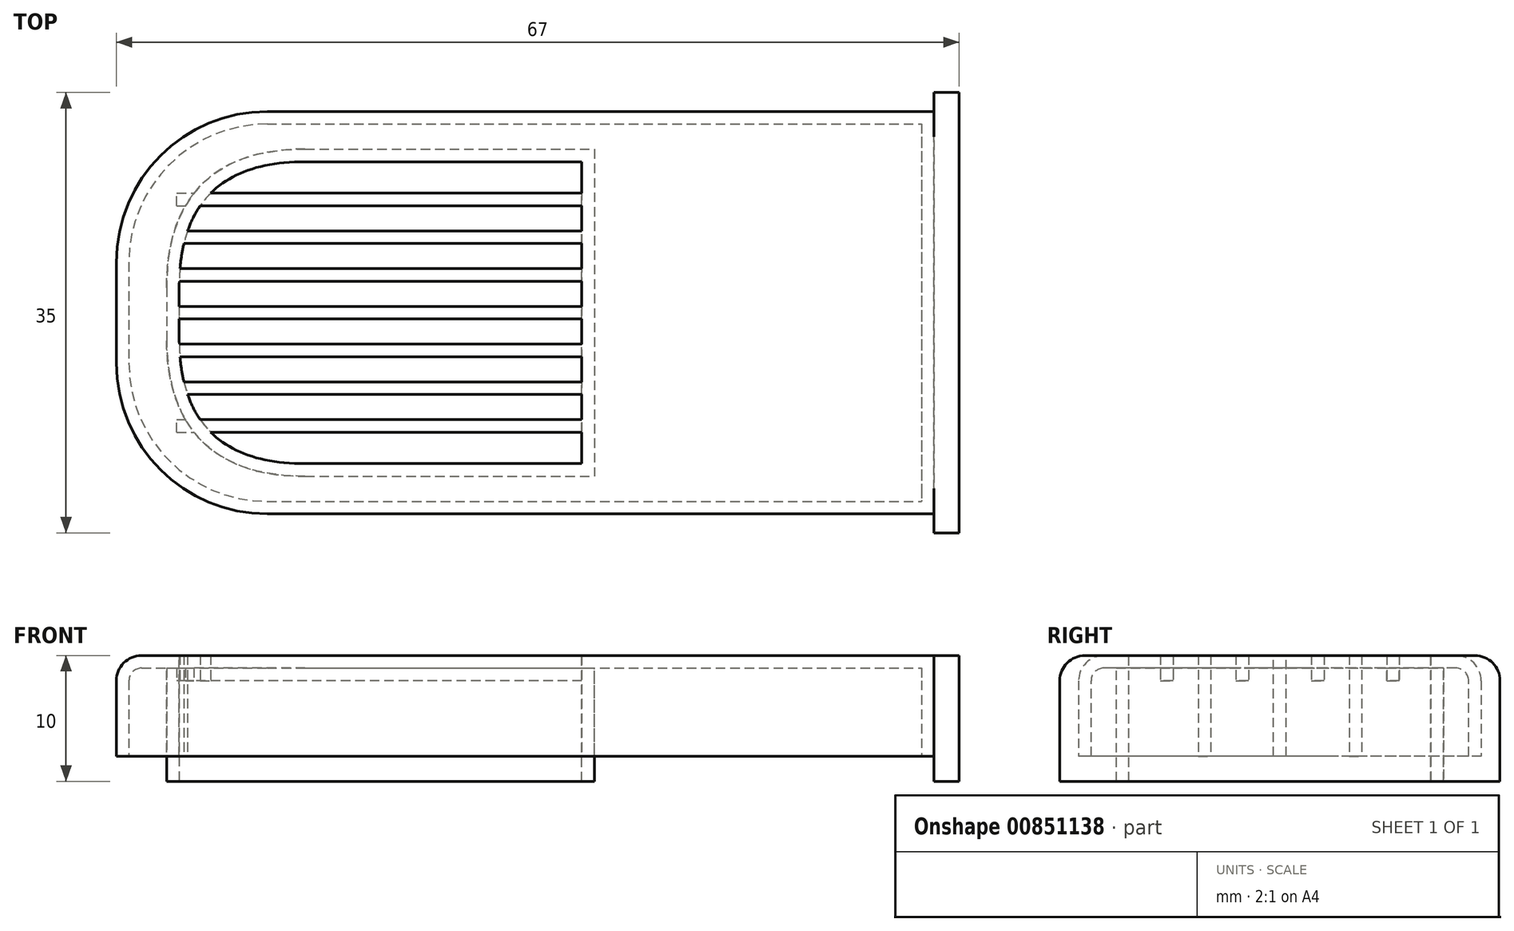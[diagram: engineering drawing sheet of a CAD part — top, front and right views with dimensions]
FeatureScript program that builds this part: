
annotation { "Feature Type Name" : "Feature", "Feature Type Description" : "" }
export const myFeature = defineFeature(function(context is Context, id is Id, definition is map)
    precondition{}
    {
        {
            var Q0;
            Q0=qCreatedBy(makeId("Top.planeOp"),FACE);
            var sketch = newSketch(context, id + "F0", { "sketchPlane" : qUnion([Q0])});
            skLineSegment(sketch, "E0.bottom", {"start": v(-32.5, 16) * mm, "end": v(32.5, 16) * mm});
            skLineSegment(sketch, "E0.top", {"start": v(-32.5, -16) * mm, "end": v(32.5, -16) * mm});
            skLineSegment(sketch, "E0.left", {"start": v(-32.5, 16) * mm, "end": v(-32.5, -16) * mm});
            skLineSegment(sketch, "E0.right", {"start": v(32.5, 16) * mm, "end": v(32.5, -16) * mm});
            skPoint(sketch, "E0.middle", {"position": v(0, 0) * mm});
            skSolve(sketch);
        }
        {
            var Q0;
            Q0=makeQuery(id+"F0.imprint","IMPRINT",FACE,{"disambiguationData":[TD([[makeQuery(id+"F0.imprint","IMPRINT",EDGE,{"derivedFrom":sQuery(id+"F0.wireOp",EDGE,"E0.bottom")}),-1.0]])]});
            extrude(context, id + "F1", {"entities" : qUnion([Q0]), "depth" : 10 * mm, "offsetDistance" : 25 * mm});
        }
        {
            var Q0;
            Q0=makeQuery(id+"F1.opExtrude","SWEPT_EDGE",EDGE,{"disambiguationData":[OSD([sQuery(id+"F0.wireOp",EDGE,"E0.bottom"),sQuery(id+"F0.wireOp",EDGE,"E0.left")])]});
            var Q1;
            Q1=makeQuery(id+"F1.opExtrude","SWEPT_EDGE",EDGE,{"disambiguationData":[OSD([sQuery(id+"F0.wireOp",EDGE,"E0.top"),sQuery(id+"F0.wireOp",EDGE,"E0.left")])]});
            fillet(context, id + "F2", {"entities" : qUnion([Q0, Q1]), "radius" : 12 * mm, "tangentPropagation" : true, "allowEdgeOverflow" : false});
        }
        {
            var Q0;
            Q0=makeQuery(id+"F1.opExtrude","CAP_FACE",FACE,{"disambiguationData":[OSD([sQuery(id+"F0.wireOp",EDGE,"E0.bottom"),sQuery(id+"F0.wireOp",EDGE,"E0.top"),sQuery(id+"F0.wireOp",EDGE,"E0.left"),sQuery(id+"F0.wireOp",EDGE,"E0.right")])],"isStart":false});
            var sketch = newSketch(context, id + "F3", { "sketchPlane" : qUnion([Q0])});
            skLineSegment(sketch, "E1.bottom", {"start": v(-27.5, 12) * mm, "end": v(4.5, 12) * mm});
            skLineSegment(sketch, "E1.top", {"start": v(-27.5, -12) * mm, "end": v(4.5, -12) * mm});
            skLineSegment(sketch, "E1.left", {"start": v(-27.5, 12) * mm, "end": v(-27.5, -12) * mm});
            skLineSegment(sketch, "E1.right", {"start": v(4.5, 12) * mm, "end": v(4.5, -12) * mm});
            skPoint(sketch, "E1.middle", {"position": v(-11.5, 0) * mm});
            skSolve(sketch);
        }
        {
            var Q0;
            Q0=makeQuery(id+"F3.imprint","IMPRINT",FACE,{"disambiguationData":[TD([[makeQuery(id+"F3.imprint","IMPRINT",EDGE,{"derivedFrom":sQuery(id+"F3.wireOp",EDGE,"E1.bottom")}),-1.0]])]});
            extrude(context, id + "F4", {"entities" : qUnion([Q0]), "operationType" : NewBodyOperationType.REMOVE, "oppositeDirection" : true, "depth" : 25 * mm, "offsetDistance" : 25 * mm});
        }
        {
            var Q0;
            Q0=makeQuery(id+"F4.boolean.opBoolean","COPY",EDGE,{"derivedFrom":makeQuery(id+"F4.opExtrude","SWEPT_EDGE",EDGE,{"disambiguationData":[OSD([sQuery(id+"F3.wireOp",EDGE,"E1.bottom"),sQuery(id+"F3.wireOp",EDGE,"E1.left")])]})});
            var Q1;
            Q1=makeQuery(id+"F4.boolean.opBoolean","COPY",EDGE,{"derivedFrom":makeQuery(id+"F4.opExtrude","SWEPT_EDGE",EDGE,{"disambiguationData":[OSD([sQuery(id+"F3.wireOp",EDGE,"E1.top"),sQuery(id+"F3.wireOp",EDGE,"E1.left")])]})});
            fillet(context, id + "F5", {"entities" : qUnion([Q0, Q1]), "radius" : 10 * mm, "tangentPropagation" : true, "rho" : 0.5, "crossSection" : FilletCrossSection.CONIC, "allowEdgeOverflow" : false});
        }
        {
            var Q0;
            Q0=makeQuery(id+"F1.opExtrude","CAP_EDGE",EDGE,{"disambiguationData":[OSD([sQuery(id+"F0.wireOp",EDGE,"E0.top")])],"isStart":false});
            var Q1;
            {var subQ0=sQuery(id+"F0.wireOp",EDGE,"E0.left");var subQ1=sQuery(id+"F0.wireOp",EDGE,"E0.top");Q1=makeQuery(id+"F2.opFillet","BLEND_EDGE",EDGE,{"blendedFrom":[makeQuery(id+"F1.opExtrude","SWEPT_EDGE",EDGE,{"disambiguationData":[OSD([subQ1,subQ0])]}),makeQuery(id+"F1.opExtrude","CAP_FACE",FACE,{"disambiguationData":[OSD([sQuery(id+"F0.wireOp",EDGE,"E0.bottom"),subQ1,subQ0,sQuery(id+"F0.wireOp",EDGE,"E0.right")])],"isStart":false})],"blendedInto":[makeQuery(id+"F1.opExtrude","CAP_FACE",FACE,{"disambiguationData":[OSD([sQuery(id+"F0.wireOp",EDGE,"E0.bottom"),subQ1,subQ0,sQuery(id+"F0.wireOp",EDGE,"E0.right")])],"isStart":false})]});}
            var Q2;
            Q2=makeQuery(id+"F1.opExtrude","CAP_EDGE",EDGE,{"disambiguationData":[OSD([sQuery(id+"F0.wireOp",EDGE,"E0.left")])],"isStart":false});
            var Q3;
            {var subQ0=sQuery(id+"F0.wireOp",EDGE,"E0.left");var subQ1=sQuery(id+"F0.wireOp",EDGE,"E0.bottom");Q3=makeQuery(id+"F2.opFillet","BLEND_EDGE",EDGE,{"blendedFrom":[makeQuery(id+"F1.opExtrude","SWEPT_EDGE",EDGE,{"disambiguationData":[OSD([subQ1,subQ0])]}),makeQuery(id+"F1.opExtrude","CAP_FACE",FACE,{"disambiguationData":[OSD([subQ1,sQuery(id+"F0.wireOp",EDGE,"E0.top"),subQ0,sQuery(id+"F0.wireOp",EDGE,"E0.right")])],"isStart":false})],"blendedInto":[makeQuery(id+"F1.opExtrude","CAP_FACE",FACE,{"disambiguationData":[OSD([subQ1,sQuery(id+"F0.wireOp",EDGE,"E0.top"),subQ0,sQuery(id+"F0.wireOp",EDGE,"E0.right")])],"isStart":false})]});}
            var Q4;
            Q4=makeQuery(id+"F1.opExtrude","CAP_EDGE",EDGE,{"disambiguationData":[OSD([sQuery(id+"F0.wireOp",EDGE,"E0.bottom")])],"isStart":false});
            fillet(context, id + "F6", {"entities" : qUnion([Q0, Q1, Q2, Q3, Q4]), "radius" : 2 * mm, "tangentPropagation" : true, "allowEdgeOverflow" : false});
        }
        {
            var Q0;
            Q0=makeQuery(id+"F1.opExtrude","CAP_FACE",FACE,{"disambiguationData":[OSD([sQuery(id+"F0.wireOp",EDGE,"E0.bottom"),sQuery(id+"F0.wireOp",EDGE,"E0.top"),sQuery(id+"F0.wireOp",EDGE,"E0.left"),sQuery(id+"F0.wireOp",EDGE,"E0.right")])],"isStart":false});
            var sketch = newSketch(context, id + "F7", { "sketchPlane" : qUnion([Q0])});
            skLineSegment(sketch, "E2", {"start": v(4.5, -9) * mm, "end": v(-27.7, -9) * mm});
            skLineSegment(sketch, "E3.0.1.0", {"start": v(4.5, -6) * mm, "end": v(-27.7, -6) * mm});
            skLineSegment(sketch, "E3.0.2.0", {"start": v(4.5, -3) * mm, "end": v(-27.7, -3) * mm});
            skLineSegment(sketch, "E3.0.3.0", {"start": v(4.5, 0) * mm, "end": v(-27.7, 0) * mm});
            skLineSegment(sketch, "E3.0.4.0", {"start": v(4.5, 3) * mm, "end": v(-27.7, 3) * mm});
            skLineSegment(sketch, "E3.0.5.0", {"start": v(4.5, 6) * mm, "end": v(-27.7, 6) * mm});
            skLineSegment(sketch, "E3.0.6.0", {"start": v(4.5, 9) * mm, "end": v(-27.7, 9) * mm});
            skLineSegment(sketch, "E3.direction1", {"start": v(-27.7, -9) * mm, "end": v(-5.14, -9) * mm, "construction": true});
            skLineSegment(sketch, "E3.direction2", {"start": v(-27.7, -9) * mm, "end": v(-27.7, -6) * mm, "construction": true});
            skSolve(sketch);
        }
        {
            var Q0;
            Q0=sQuery(id+"F7.wireOp",EDGE,"E3.0.1.0");
            var Q1;
            Q1=sQuery(id+"F7.wireOp",EDGE,"E3.0.3.0");
            var Q2;
            Q2=sQuery(id+"F7.wireOp",EDGE,"E3.0.5.0");
            extrude(context, id + "F8", {"bodyType" : ToolBodyType.SURFACE, "surfaceEntities" : qUnion([Q0, Q1, Q2]), "oppositeDirection" : true, "depth" : 8 * mm, "offsetDistance" : 25 * mm});
        }
        {
            var Q0;
            Q0=sQuery(id+"F7.wireOp",EDGE,"E3.0.2.0");
            var Q1;
            Q1=sQuery(id+"F7.wireOp",EDGE,"E3.0.4.0");
            var Q2;
            Q2=sQuery(id+"F7.wireOp",EDGE,"E3.0.6.0");
            var Q3;
            Q3=sQuery(id+"F7.wireOp",EDGE,"E2");
            extrude(context, id + "F9", {"bodyType" : ToolBodyType.SURFACE, "surfaceEntities" : qUnion([Q0, Q1, Q2, Q3]), "oppositeDirection" : true, "depth" : 2 * mm, "offsetDistance" : 25 * mm});
        }
        {
            var Q0;
            Q0=makeQuery(id+"F1.opExtrude","CAP_FACE",FACE,{"disambiguationData":[OSD([sQuery(id+"F0.wireOp",EDGE,"E0.bottom"),sQuery(id+"F0.wireOp",EDGE,"E0.top"),sQuery(id+"F0.wireOp",EDGE,"E0.left"),sQuery(id+"F0.wireOp",EDGE,"E0.right")])],"isStart":true});
            shell(context, id + "F10", {"entities" : qUnion([Q0]), "thickness" : 1 * mm});
        }
        {
            var Q0;
            Q0=makeQuery(id+"F8.opExtrude","SWEPT_FACE",FACE,{"disambiguationData":[OSD([sQuery(id+"F7.wireOp",EDGE,"E3.0.5.0")])]});
            var Q1;
            Q1=makeQuery(id+"F8.opExtrude","SWEPT_FACE",FACE,{"disambiguationData":[OSD([sQuery(id+"F7.wireOp",EDGE,"E3.0.3.0")])]});
            var Q2;
            Q2=makeQuery(id+"F8.opExtrude","SWEPT_FACE",FACE,{"disambiguationData":[OSD([sQuery(id+"F7.wireOp",EDGE,"E3.0.1.0")])]});
            var Q3;
            Q3=makeQuery(id+"F9.opExtrude","SWEPT_FACE",FACE,{"disambiguationData":[OSD([sQuery(id+"F7.wireOp",EDGE,"E2")])]});
            var Q4;
            Q4=makeQuery(id+"F9.opExtrude","SWEPT_FACE",FACE,{"disambiguationData":[OSD([sQuery(id+"F7.wireOp",EDGE,"E3.0.2.0")])]});
            var Q5;
            Q5=makeQuery(id+"F9.opExtrude","SWEPT_FACE",FACE,{"disambiguationData":[OSD([sQuery(id+"F7.wireOp",EDGE,"E3.0.4.0")])]});
            var Q6;
            Q6=makeQuery(id+"F9.opExtrude","SWEPT_FACE",FACE,{"disambiguationData":[OSD([sQuery(id+"F7.wireOp",EDGE,"E3.0.6.0")])]});
            extrude(context, id + "F11", {"entities" : qUnion([Q0, Q1, Q2, Q3, Q4, Q5, Q6]), "operationType" : NewBodyOperationType.ADD, "endBound" : BoundingType.SYMMETRIC, "depth" : 1 * mm, "offsetDistance" : 25 * mm});
        }
        {
            var Q0;
            {var subQ0=sQuery(id+"F0.wireOp",EDGE,"E0.right");var subQ1=sQuery(id+"F0.wireOp",EDGE,"E0.left");var subQ2=sQuery(id+"F0.wireOp",EDGE,"E0.top");var subQ3=sQuery(id+"F0.wireOp",EDGE,"E0.bottom");Q0=makeQuery(id+"F10.opShell","OFFSET_FACE",FACE,{"disambiguationData":[OSD([subQ3,subQ2,subQ1,subQ0]),TDD([makeQuery(id+"F1.opExtrude","CAP_FACE",FACE,{"disambiguationData":[OSD([subQ3,subQ2,subQ1,subQ0])],"isStart":true})])]});}
            extrude(context, id + "F12", {"entities" : qUnion([Q0]), "operationType" : NewBodyOperationType.REMOVE, "oppositeDirection" : true, "depth" : 2 * mm, "offsetDistance" : 25 * mm});
        }
        {
            var Q0;
            Q0=makeQuery(id+"F1.opExtrude","SWEPT_FACE",FACE,{"disambiguationData":[OSD([sQuery(id+"F0.wireOp",EDGE,"E0.right")])]});
            var sketch = newSketch(context, id + "F13", { "sketchPlane" : qUnion([Q0])});
            skLineSegment(sketch, "E4.bottom", {"start": v(-17.5, 10) * mm, "end": v(17.5, 10) * mm});
            skLineSegment(sketch, "E4.top", {"start": v(-17.5, 0) * mm, "end": v(17.5, 0) * mm});
            skLineSegment(sketch, "E4.left", {"start": v(-17.5, 10) * mm, "end": v(-17.5, 0) * mm});
            skLineSegment(sketch, "E4.right", {"start": v(17.5, 10) * mm, "end": v(17.5, 0) * mm});
            skPoint(sketch, "E4.middle", {"position": v(0, 5) * mm});
            skSolve(sketch);
        }
        {
            var Q0;
            {var subQ3=sQuery(id+"F13.wireOp",EDGE,"E4.left");Q0=makeQuery(id+"F13.imprint","IMPRINT",FACE,{"disambiguationData":[TD([[makeQuery(id+"F13.imprint","IMPRINT",EDGE,{"derivedFrom":subQ3}),1.0]])]});}
            var Q1;
            {var subQ0=sQuery(id+"F0.wireOp",EDGE,"E0.right");var subQ1=sQuery(id+"F0.wireOp",EDGE,"E0.bottom");var subQ2=makeQuery(id+"F1.opExtrude","SWEPT_EDGE",EDGE,{"disambiguationData":[OSD([subQ1,subQ0])]});Q1=makeQuery(id+"F13.imprint","IMPRINT",FACE,{"disambiguationData":[TD([[makeQuery(id+"F13.imprint","IMPRINT",EDGE,{"derivedFrom":subQ2}),-1.0]])]});}
            var Q2;
            {var subQ4=sQuery(id+"F13.wireOp",EDGE,"E4.right");Q2=makeQuery(id+"F13.imprint","IMPRINT",FACE,{"disambiguationData":[TD([[makeQuery(id+"F13.imprint","IMPRINT",EDGE,{"derivedFrom":subQ4}),-1.0]])]});}
            extrude(context, id + "F14", {"entities" : qUnion([Q0, Q1, Q2]), "operationType" : NewBodyOperationType.ADD, "depth" : 2 * mm, "offsetDistance" : 25 * mm});
        }
        {
            var Q0;
            Q0=makeQuery(id+"F14.opExtrude","SWEPT_EDGE",EDGE,{"disambiguationData":[OSD([sQuery(id+"F13.wireOp",EDGE,"E4.bottom"),sQuery(id+"F13.wireOp",EDGE,"E4.right")])]});
            var Q1;
            Q1=makeQuery(id+"F14.opExtrude","SWEPT_EDGE",EDGE,{"disambiguationData":[OSD([sQuery(id+"F13.wireOp",EDGE,"E4.bottom"),sQuery(id+"F13.wireOp",EDGE,"E4.left")])]});
            fillet(context, id + "F15", {"entities" : qUnion([Q0, Q1]), "radius" : 2 * mm, "tangentPropagation" : true, "allowEdgeOverflow" : false});
        }
    });
